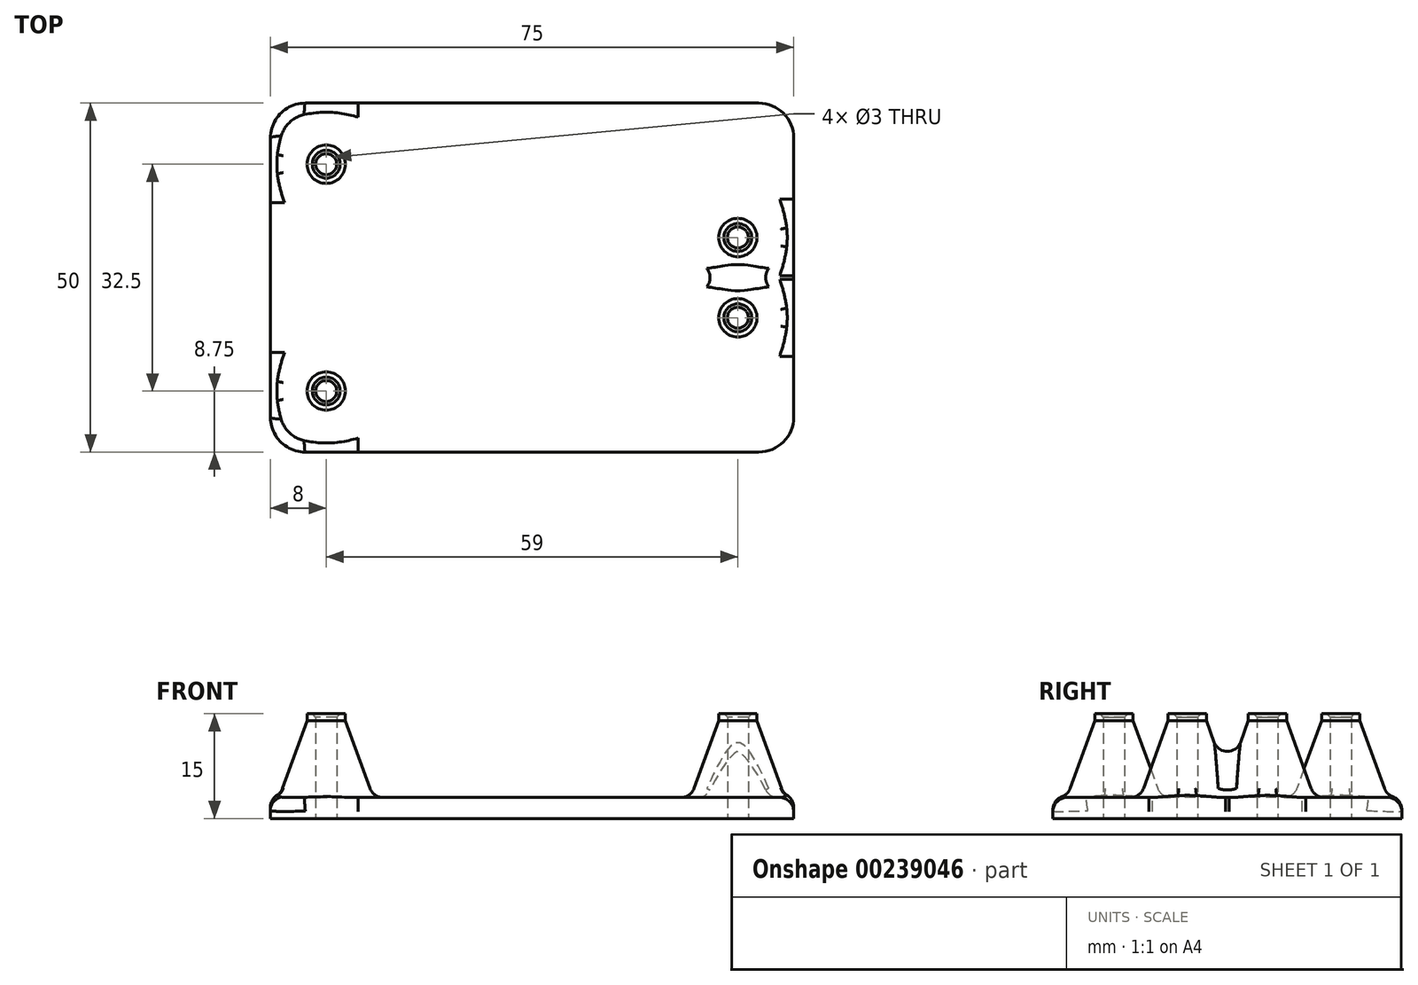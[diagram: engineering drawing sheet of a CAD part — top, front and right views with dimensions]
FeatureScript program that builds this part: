
annotation { "Feature Type Name" : "Feature", "Feature Type Description" : "" }
export const myFeature = defineFeature(function(context is Context, id is Id, definition is map)
    precondition{}
    {
        {
            var Q0;
            Q0=qCreatedBy(makeId("Top.planeOp"),FACE);
            var sketch = newSketch(context, id + "F0", { "sketchPlane" : qUnion([Q0])});
            skCircle(sketch, "E0", {"center": v(-29.5, 16.25) * mm, "radius": 1.5 * mm});
            skCircle(sketch, "E1", {"center": v(29.5, 5.75) * mm, "radius": 1.5 * mm});
            skLineSegment(sketch, "E2", {"start": v(0, 0) * mm, "end": v(-59.39, 0) * mm, "construction": true});
            skLineSegment(sketch, "E3", {"start": v(0, 0) * mm, "end": v(59.46, 0) * mm, "construction": true});
            skLineSegment(sketch, "E4.bottom", {"start": v(37.5, 25) * mm, "end": v(-37.5, 25) * mm});
            skLineSegment(sketch, "E4.top", {"start": v(37.5, -25) * mm, "end": v(-37.5, -25) * mm});
            skLineSegment(sketch, "E4.left", {"start": v(37.5, 25) * mm, "end": v(37.5, -25) * mm});
            skLineSegment(sketch, "E4.right", {"start": v(-37.5, 25) * mm, "end": v(-37.5, -25) * mm});
            skPoint(sketch, "E4.middle", {"position": v(0, 0) * mm});
            skCircle(sketch, "E5.MirrorC", {"center": v(-29.5, -16.25) * mm, "radius": 1.5 * mm});
            skCircle(sketch, "E6.MirrorC", {"center": v(29.5, -5.75) * mm, "radius": 1.5 * mm});
            skSolve(sketch);
        }
        {
            var Q0;
            Q0 = qSketchRegion(id + "F0", true);
            extrude(context, id + "F1", {"entities" : qUnion([Q0]), "depth" : 3 * mm});
        }
        {
            var Q0;
            Q0=qCreatedBy(makeId("Top.planeOp"),FACE);
            var sketch = newSketch(context, id + "F2", { "sketchPlane" : qUnion([Q0])});
            skCircle(sketch, "E7.0", {"center": v(-29.5, 16.25) * mm, "radius": 1.5 * mm});
            skCircle(sketch, "E8.0", {"center": v(-29.5, -16.25) * mm, "radius": 1.5 * mm});
            skCircle(sketch, "E9.0", {"center": v(29.5, -5.75) * mm, "radius": 1.5 * mm});
            skCircle(sketch, "E10.0", {"center": v(29.5, 5.75) * mm, "radius": 1.5 * mm});
            skCircle(sketch, "E11", {"center": v(-29.5, 16.25) * mm, "radius": 2.75 * mm});
            skCircle(sketch, "E12", {"center": v(-29.5, -16.25) * mm, "radius": 2.75 * mm});
            skCircle(sketch, "E13", {"center": v(29.5, -5.75) * mm, "radius": 2.75 * mm});
            skCircle(sketch, "E14", {"center": v(29.5, 5.75) * mm, "radius": 2.75 * mm});
            skSolve(sketch);
        }
        {
            var Q0;
            Q0 = qSketchRegion(id + "F2", true);
            extrude(context, id + "F3", {"entities" : qUnion([Q0]), "operationType" : NewBodyOperationType.ADD, "offsetDistance" : 25 * mm, "depth" : 15 * mm});
        }
        {
            var Q0;
            Q0=makeQuery(id+"F3.boolean.opBoolean","INTERSECT",EDGE,{"derivedFrom":[makeQuery(id+"F1.opExtrude","CAP_FACE",FACE,{"disambiguationData":[OSD([sQuery(id+"F0.wireOp",EDGE,"E0"),sQuery(id+"F0.wireOp",EDGE,"E1"),sQuery(id+"F0.wireOp",EDGE,"E4.bottom"),sQuery(id+"F0.wireOp",EDGE,"E4.top"),sQuery(id+"F0.wireOp",EDGE,"E4.left"),sQuery(id+"F0.wireOp",EDGE,"E4.right"),sQuery(id+"F0.wireOp",EDGE,"E5.MirrorC"),sQuery(id+"F0.wireOp",EDGE,"E6.MirrorC")])],"isStart":false}),makeQuery(id+"F3.opExtrude","SWEPT_FACE",FACE,{"disambiguationData":[OSD([sQuery(id+"F2.wireOp",EDGE,"E12")])]})]});
            var Q1;
            Q1=makeQuery(id+"F3.boolean.opBoolean","INTERSECT",EDGE,{"derivedFrom":[makeQuery(id+"F1.opExtrude","CAP_FACE",FACE,{"disambiguationData":[OSD([sQuery(id+"F0.wireOp",EDGE,"E0"),sQuery(id+"F0.wireOp",EDGE,"E1"),sQuery(id+"F0.wireOp",EDGE,"E4.bottom"),sQuery(id+"F0.wireOp",EDGE,"E4.top"),sQuery(id+"F0.wireOp",EDGE,"E4.left"),sQuery(id+"F0.wireOp",EDGE,"E4.right"),sQuery(id+"F0.wireOp",EDGE,"E5.MirrorC"),sQuery(id+"F0.wireOp",EDGE,"E6.MirrorC")])],"isStart":false}),makeQuery(id+"F3.opExtrude","SWEPT_FACE",FACE,{"disambiguationData":[OSD([sQuery(id+"F2.wireOp",EDGE,"E11")])]})]});
            var Q2;
            Q2=makeQuery(id+"F3.boolean.opBoolean","INTERSECT",EDGE,{"derivedFrom":[makeQuery(id+"F1.opExtrude","CAP_FACE",FACE,{"disambiguationData":[OSD([sQuery(id+"F0.wireOp",EDGE,"E0"),sQuery(id+"F0.wireOp",EDGE,"E1"),sQuery(id+"F0.wireOp",EDGE,"E4.bottom"),sQuery(id+"F0.wireOp",EDGE,"E4.top"),sQuery(id+"F0.wireOp",EDGE,"E4.left"),sQuery(id+"F0.wireOp",EDGE,"E4.right"),sQuery(id+"F0.wireOp",EDGE,"E5.MirrorC"),sQuery(id+"F0.wireOp",EDGE,"E6.MirrorC")])],"isStart":false}),makeQuery(id+"F3.opExtrude","SWEPT_FACE",FACE,{"disambiguationData":[OSD([sQuery(id+"F2.wireOp",EDGE,"E13")])]})]});
            var Q3;
            Q3=makeQuery(id+"F3.boolean.opBoolean","INTERSECT",EDGE,{"derivedFrom":[makeQuery(id+"F1.opExtrude","CAP_FACE",FACE,{"disambiguationData":[OSD([sQuery(id+"F0.wireOp",EDGE,"E0"),sQuery(id+"F0.wireOp",EDGE,"E1"),sQuery(id+"F0.wireOp",EDGE,"E4.bottom"),sQuery(id+"F0.wireOp",EDGE,"E4.top"),sQuery(id+"F0.wireOp",EDGE,"E4.left"),sQuery(id+"F0.wireOp",EDGE,"E4.right"),sQuery(id+"F0.wireOp",EDGE,"E5.MirrorC"),sQuery(id+"F0.wireOp",EDGE,"E6.MirrorC")])],"isStart":false}),makeQuery(id+"F3.opExtrude","SWEPT_FACE",FACE,{"disambiguationData":[OSD([sQuery(id+"F2.wireOp",EDGE,"E14")])]})]});
            chamfer(context, id + "F4", {"entities" : qUnion([Q0, Q1, Q2, Q3]), "chamferType" : ChamferType.TWO_OFFSETS, "width1" : 4 * mm, "oppositeDirection" : false, "width2" : 11 * mm, "tangentPropagation" : true});
        }
        {
            var Q0;
            {var subQ0=makeQuery(id+"F1.opExtrude","CAP_FACE",FACE,{"disambiguationData":[OSD([sQuery(id+"F0.wireOp",EDGE,"E0"),sQuery(id+"F0.wireOp",EDGE,"E1"),sQuery(id+"F0.wireOp",EDGE,"E4.bottom"),sQuery(id+"F0.wireOp",EDGE,"E4.top"),sQuery(id+"F0.wireOp",EDGE,"E4.left"),sQuery(id+"F0.wireOp",EDGE,"E4.right"),sQuery(id+"F0.wireOp",EDGE,"E5.MirrorC"),sQuery(id+"F0.wireOp",EDGE,"E6.MirrorC")])],"isStart":false});Q0=makeQuery(id+"F4.opChamfer","BLEND_EDGE",EDGE,{"blendedFrom":[makeQuery(id+"F3.boolean.opBoolean","INTERSECT",EDGE,{"derivedFrom":[subQ0,makeQuery(id+"F3.opExtrude","SWEPT_FACE",FACE,{"disambiguationData":[OSD([sQuery(id+"F2.wireOp",EDGE,"E11")])]})]}),subQ0],"blendedInto":[subQ0]});}
            var Q1;
            {var subQ0=makeQuery(id+"F1.opExtrude","CAP_FACE",FACE,{"disambiguationData":[OSD([sQuery(id+"F0.wireOp",EDGE,"E0"),sQuery(id+"F0.wireOp",EDGE,"E1"),sQuery(id+"F0.wireOp",EDGE,"E4.bottom"),sQuery(id+"F0.wireOp",EDGE,"E4.top"),sQuery(id+"F0.wireOp",EDGE,"E4.left"),sQuery(id+"F0.wireOp",EDGE,"E4.right"),sQuery(id+"F0.wireOp",EDGE,"E5.MirrorC"),sQuery(id+"F0.wireOp",EDGE,"E6.MirrorC")])],"isStart":false});Q1=makeQuery(id+"F4.opChamfer","BLEND_EDGE",EDGE,{"blendedFrom":[makeQuery(id+"F3.boolean.opBoolean","INTERSECT",EDGE,{"derivedFrom":[subQ0,makeQuery(id+"F3.opExtrude","SWEPT_FACE",FACE,{"disambiguationData":[OSD([sQuery(id+"F2.wireOp",EDGE,"E12")])]})]}),subQ0],"blendedInto":[subQ0]});}
            var Q2;
            {var subQ0=makeQuery(id+"F1.opExtrude","CAP_FACE",FACE,{"disambiguationData":[OSD([sQuery(id+"F0.wireOp",EDGE,"E0"),sQuery(id+"F0.wireOp",EDGE,"E1"),sQuery(id+"F0.wireOp",EDGE,"E4.bottom"),sQuery(id+"F0.wireOp",EDGE,"E4.top"),sQuery(id+"F0.wireOp",EDGE,"E4.left"),sQuery(id+"F0.wireOp",EDGE,"E4.right"),sQuery(id+"F0.wireOp",EDGE,"E5.MirrorC"),sQuery(id+"F0.wireOp",EDGE,"E6.MirrorC")])],"isStart":false});Q2=makeQuery(id+"F4.opChamfer","BLEND_EDGE",EDGE,{"blendedFrom":[makeQuery(id+"F3.boolean.opBoolean","INTERSECT",EDGE,{"derivedFrom":[subQ0,makeQuery(id+"F3.opExtrude","SWEPT_FACE",FACE,{"disambiguationData":[OSD([sQuery(id+"F2.wireOp",EDGE,"E13")])]})]}),subQ0],"blendedInto":[subQ0]});}
            var Q3;
            {var subQ0=makeQuery(id+"F1.opExtrude","CAP_FACE",FACE,{"disambiguationData":[OSD([sQuery(id+"F0.wireOp",EDGE,"E0"),sQuery(id+"F0.wireOp",EDGE,"E1"),sQuery(id+"F0.wireOp",EDGE,"E4.bottom"),sQuery(id+"F0.wireOp",EDGE,"E4.top"),sQuery(id+"F0.wireOp",EDGE,"E4.left"),sQuery(id+"F0.wireOp",EDGE,"E4.right"),sQuery(id+"F0.wireOp",EDGE,"E5.MirrorC"),sQuery(id+"F0.wireOp",EDGE,"E6.MirrorC")])],"isStart":false});Q3=makeQuery(id+"F4.opChamfer","BLEND_EDGE",EDGE,{"blendedFrom":[makeQuery(id+"F3.boolean.opBoolean","INTERSECT",EDGE,{"derivedFrom":[subQ0,makeQuery(id+"F3.opExtrude","SWEPT_FACE",FACE,{"disambiguationData":[OSD([sQuery(id+"F2.wireOp",EDGE,"E14")])]})]}),subQ0],"blendedInto":[subQ0]});}
            var Q4;
            {var subQ0=makeQuery(id+"F1.opExtrude","CAP_FACE",FACE,{"disambiguationData":[OSD([sQuery(id+"F0.wireOp",EDGE,"E0"),sQuery(id+"F0.wireOp",EDGE,"E1"),sQuery(id+"F0.wireOp",EDGE,"E4.bottom"),sQuery(id+"F0.wireOp",EDGE,"E4.top"),sQuery(id+"F0.wireOp",EDGE,"E4.left"),sQuery(id+"F0.wireOp",EDGE,"E4.right"),sQuery(id+"F0.wireOp",EDGE,"E5.MirrorC"),sQuery(id+"F0.wireOp",EDGE,"E6.MirrorC")])],"isStart":false});Q4=makeQuery(id+"F4.opChamfer","BLEND_EDGE",EDGE,{"blendedFrom":[makeQuery(id+"F3.boolean.opBoolean","INTERSECT",EDGE,{"derivedFrom":[subQ0,makeQuery(id+"F3.opExtrude","SWEPT_FACE",FACE,{"disambiguationData":[OSD([sQuery(id+"F2.wireOp",EDGE,"E13")])]})]}),makeQuery(id+"F3.boolean.opBoolean","INTERSECT",EDGE,{"derivedFrom":[subQ0,makeQuery(id+"F3.opExtrude","SWEPT_FACE",FACE,{"disambiguationData":[OSD([sQuery(id+"F2.wireOp",EDGE,"E14")])]})]})],"blendedInto":[]});}
            fillet(context, id + "F5", {"entities" : qUnion([Q0, Q1, Q2, Q3, Q4]), "radius" : 2 * mm, "tangentPropagation" : true, "allowEdgeOverflow" : false});
        }
        {
            var Q0;
            Q0=makeQuery(id+"F3.opExtrude","CAP_EDGE",EDGE,{"disambiguationData":[OSD([sQuery(id+"F2.wireOp",EDGE,"E8.0")])],"isStart":false});
            var Q1;
            Q1=makeQuery(id+"F3.opExtrude","CAP_EDGE",EDGE,{"disambiguationData":[OSD([sQuery(id+"F2.wireOp",EDGE,"E9.0")])],"isStart":false});
            var Q2;
            Q2=makeQuery(id+"F3.opExtrude","CAP_EDGE",EDGE,{"disambiguationData":[OSD([sQuery(id+"F2.wireOp",EDGE,"E10.0")])],"isStart":false});
            var Q3;
            Q3=makeQuery(id+"F3.opExtrude","CAP_EDGE",EDGE,{"disambiguationData":[OSD([sQuery(id+"F2.wireOp",EDGE,"E7.0")])],"isStart":false});
            chamfer(context, id + "F6", {"entities" : qUnion([Q0, Q1, Q2, Q3]), "width" : 0.5 * mm, "tangentPropagation" : true});
        }
        {
            var Q0;
            Q0=makeQuery(id+"F1.opExtrude","SWEPT_EDGE",EDGE,{"disambiguationData":[OSD([sQuery(id+"F0.wireOp",EDGE,"E4.top"),sQuery(id+"F0.wireOp",EDGE,"E4.right")])]});
            var Q1;
            Q1=makeQuery(id+"F1.opExtrude","SWEPT_EDGE",EDGE,{"disambiguationData":[OSD([sQuery(id+"F0.wireOp",EDGE,"E4.top"),sQuery(id+"F0.wireOp",EDGE,"E4.left")])]});
            var Q2;
            Q2=makeQuery(id+"F1.opExtrude","SWEPT_EDGE",EDGE,{"disambiguationData":[OSD([sQuery(id+"F0.wireOp",EDGE,"E4.bottom"),sQuery(id+"F0.wireOp",EDGE,"E4.left")])]});
            var Q3;
            Q3=makeQuery(id+"F1.opExtrude","SWEPT_EDGE",EDGE,{"disambiguationData":[OSD([sQuery(id+"F0.wireOp",EDGE,"E4.bottom"),sQuery(id+"F0.wireOp",EDGE,"E4.right")])]});
            fillet(context, id + "F7", {"entities" : qUnion([Q0, Q1, Q2, Q3]), "radius" : 5 * mm, "tangentPropagation" : true, "allowEdgeOverflow" : false});
        }
        {
            var Q0;
            Q0=makeQuery(id+"F1.opExtrude","CAP_EDGE",EDGE,{"disambiguationData":[OSD([sQuery(id+"F0.wireOp",EDGE,"E4.bottom")])],"isStart":false});
            fillet(context, id + "F8", {"entities" : qUnion([Q0]), "radius" : 2 * mm, "tangentPropagation" : true, "allowEdgeOverflow" : false});
        }
    });
